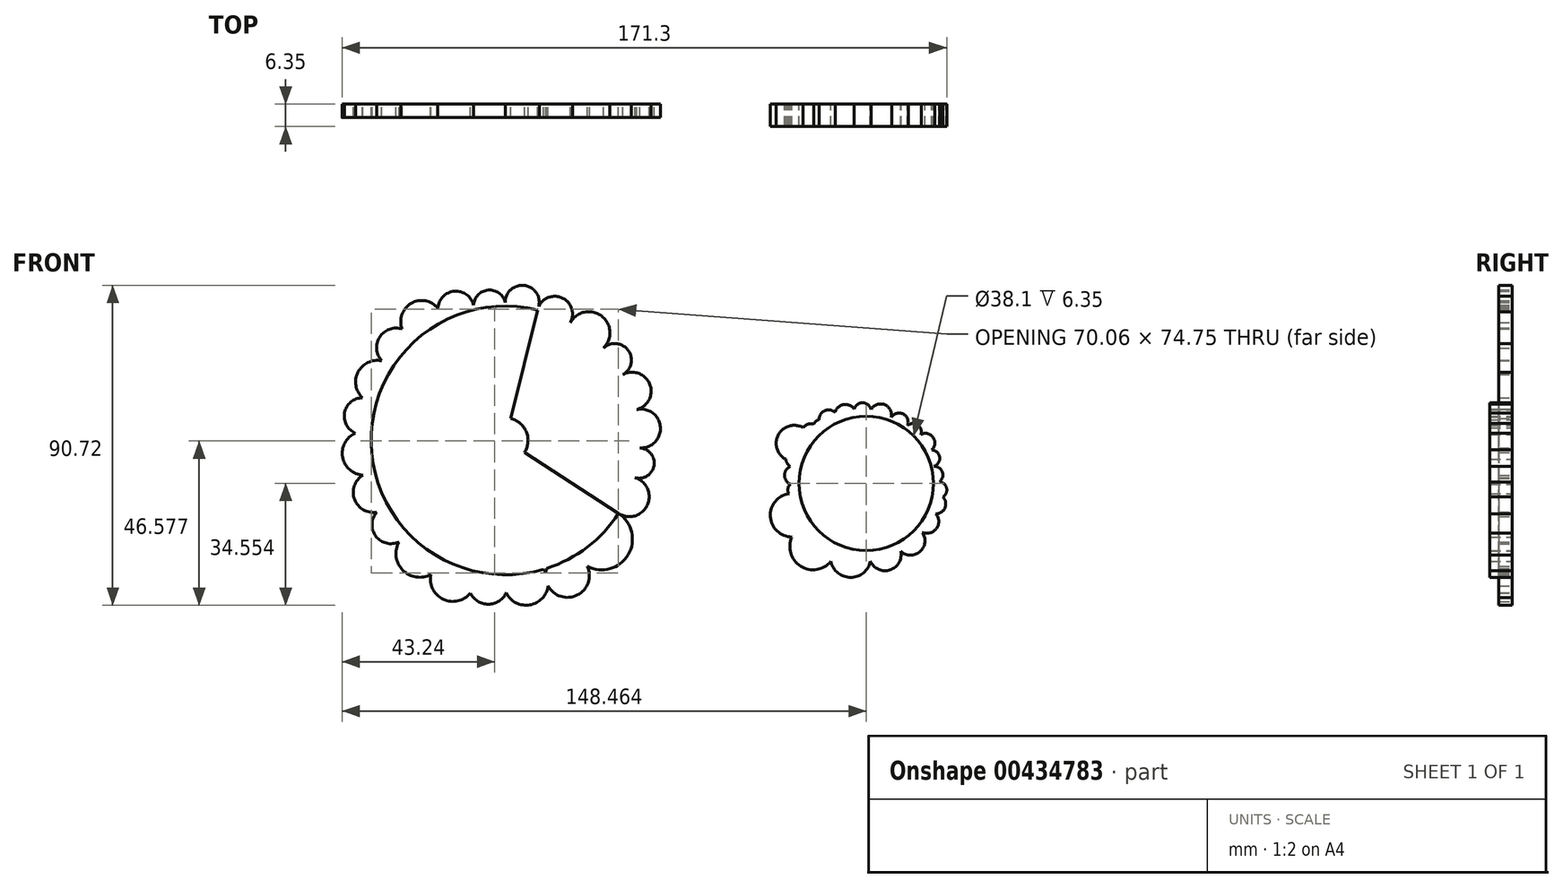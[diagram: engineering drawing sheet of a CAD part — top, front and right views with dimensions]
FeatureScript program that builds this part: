
annotation { "Feature Type Name" : "Feature", "Feature Type Description" : "" }
export const myFeature = defineFeature(function(context is Context, id is Id, definition is map)
    precondition{}
    {
        {
            var Q0;
            Q0=qCreatedBy(makeId("Front.planeOp"),FACE);
            var sketch = newSketch(context, id + "F0", { "sketchPlane" : qUnion([Q0])});
            skCircle(sketch, "E0", {"center": v(-53.83, 43.14) * mm, "radius": 38.1 * mm});
            skCircle(sketch, "E1", {"center": v(-53.83, 43.14) * mm, "radius": 6.35 * mm});
            skLineSegment(sketch, "E2", {"start": v(-71.65, 76.82) * mm, "end": v(-53.83, 43.14) * mm});
            skLineSegment(sketch, "E3", {"start": v(-53.83, 43.14) * mm, "end": v(-34.02, 10.6) * mm});
            skLineSegment(sketch, "E4", {"start": v(-53.83, 43.14) * mm, "end": v(-62.77, 80.18) * mm});
            skLineSegment(sketch, "E5", {"start": v(-53.83, 43.14) * mm, "end": v(-43.1, 6.58) * mm});
            skLineSegment(sketch, "E6", {"start": v(-53.83, 5.04) * mm, "end": v(-53.83, 81.24) * mm});
            skLineSegment(sketch, "E7", {"start": v(-85.76, 63.93) * mm, "end": v(-21.86, 22.42) * mm});
            skLineSegment(sketch, "E8", {"start": v(-44.79, 80.15) * mm, "end": v(-62.86, 6.12) * mm});
            skLineSegment(sketch, "E9", {"start": v(-15.8, 41.02) * mm, "end": v(-91.87, 45.34) * mm});
            skLineSegment(sketch, "E10", {"start": v(-20.61, 61.8) * mm, "end": v(-87.08, 24.54) * mm});
            skLineSegment(sketch, "E11", {"start": v(-90.48, 53.55) * mm, "end": v(-17.23, 32.56) * mm});
            skLineSegment(sketch, "E12", {"start": v(-16.74, 51.85) * mm, "end": v(-90.84, 34.1) * mm});
            skLineSegment(sketch, "E13", {"start": v(-81.45, 16.9) * mm, "end": v(-26.14, 69.3) * mm});
            skLineSegment(sketch, "E14", {"start": v(-72.31, 9.82) * mm, "end": v(-35.5, 76.54) * mm});
            skArc(sketch, "E15", {"start": v(-62.77, 80.18) * mm, "mid": v(-69.71, 85.11) * mm, "end": v(-71.65, 76.82) * mm});
            skArc(sketch, "E16", {"start": v(-44.79, 80.15) * mm, "mid": v(-48.54, 87.07) * mm, "end": v(-53.83, 81.24) * mm});
            skArc(sketch, "E17", {"start": v(-26.14, 69.3) * mm, "mid": v(-26.6, 78.38) * mm, "end": v(-35.5, 76.54) * mm});
            skArc(sketch, "E18", {"start": v(-16.74, 51.85) * mm, "mid": v(-12.98, 59.04) * mm, "end": v(-20.61, 61.8) * mm});
            skArc(sketch, "E19", {"start": v(-71.65, 76.82) * mm, "mid": v(-81.02, 81.72) * mm, "end": v(-79.55, 71.25) * mm});
            skArc(sketch, "E20", {"start": v(-53.83, 81.24) * mm, "mid": v(-58.9, 85.74) * mm, "end": v(-62.77, 80.18) * mm});
            skArc(sketch, "E21", {"start": v(-35.5, 76.54) * mm, "mid": v(-38.08, 83.65) * mm, "end": v(-44.79, 80.15) * mm});
            skArc(sketch, "E22", {"start": v(-20.61, 61.8) * mm, "mid": v(-19.12, 68.68) * mm, "end": v(-26.14, 69.3) * mm});
            skArc(sketch, "E23", {"start": v(-15.8, 41.02) * mm, "mid": v(-9.98, 46.99) * mm, "end": v(-16.74, 51.85) * mm});
            skArc(sketch, "E24", {"start": v(-17.23, 32.56) * mm, "mid": v(-11.79, 35.98) * mm, "end": v(-15.8, 41.02) * mm});
            skArc(sketch, "E25", {"start": v(-21.86, 22.42) * mm, "mid": v(-13.66, 24.8) * mm, "end": v(-17.23, 32.56) * mm});
            skArc(sketch, "E26", {"start": v(-34.02, 10.6) * mm, "mid": v(-20.53, 8.9) * mm, "end": v(-21.86, 22.42) * mm});
            skArc(sketch, "E27", {"start": v(-42.15, 6.87) * mm, "mid": v(-33.7, -0.83) * mm, "end": v(-34.02, 10.6) * mm});
            skArc(sketch, "E28", {"start": v(-53.83, 5.04) * mm, "mid": v(-47.13, -3.55) * mm, "end": v(-43.1, 6.58) * mm});
            skArc(sketch, "E29", {"start": v(-62.86, 6.12) * mm, "mid": v(-59.41, -3.3) * mm, "end": v(-53.83, 5.04) * mm});
            skArc(sketch, "E30", {"start": v(-71.65, 9.46) * mm, "mid": v(-71.02, -2.12) * mm, "end": v(-62.86, 6.12) * mm});
            skArc(sketch, "E31", {"start": v(-81.45, 16.9) * mm, "mid": v(-82.23, 5.7) * mm, "end": v(-71.65, 9.46) * mm});
            skArc(sketch, "E32", {"start": v(-87.08, 24.54) * mm, "mid": v(-90.63, 16.03) * mm, "end": v(-81.45, 16.9) * mm});
            skArc(sketch, "E33", {"start": v(-90.84, 34.1) * mm, "mid": v(-96.59, 26.32) * mm, "end": v(-87.08, 24.54) * mm});
            skArc(sketch, "E34", {"start": v(-91.87, 45.34) * mm, "mid": v(-100.1, 38.92) * mm, "end": v(-90.84, 34.1) * mm});
            skArc(sketch, "E35", {"start": v(-90.48, 53.55) * mm, "mid": v(-99.47, 50.85) * mm, "end": v(-91.87, 45.34) * mm});
            skArc(sketch, "E36", {"start": v(-85.76, 63.93) * mm, "mid": v(-95.77, 62.22) * mm, "end": v(-90.48, 53.55) * mm});
            skArc(sketch, "E37", {"start": v(-79.55, 71.25) * mm, "mid": v(-89.06, 73.02) * mm, "end": v(-85.76, 63.93) * mm});
            skSolve(sketch);
        }
        {
            var Q0;
            Q0=qCreatedBy(makeId("Front.planeOp"),FACE);
            var sketch = newSketch(context, id + "F1", { "sketchPlane" : qUnion([Q0])});
            skCircle(sketch, "E38", {"center": v(48.33, 30.93) * mm, "radius": 19.05 * mm});
            skCircle(sketch, "E39", {"center": v(48.33, 30.93) * mm, "radius": 6.35 * mm});
            skArc(sketch, "E40", {"start": v(45.45, 49.76) * mm, "mid": v(41.56, 53.2) * mm, "end": v(40.24, 48.18) * mm});
            skArc(sketch, "E41", {"start": v(49.32, 49.96) * mm, "mid": v(47.18, 53.8) * mm, "end": v(45.45, 49.76) * mm});
            skArc(sketch, "E42", {"start": v(55.07, 48.75) * mm, "mid": v(53.04, 53.4) * mm, "end": v(49.32, 49.96) * mm});
            skArc(sketch, "E43", {"start": v(59.41, 46.43) * mm, "mid": v(58.84, 50.59) * mm, "end": v(55.07, 48.75) * mm});
            skArc(sketch, "E44", {"start": v(62.66, 43.5) * mm, "mid": v(63.18, 47.33) * mm, "end": v(59.41, 46.43) * mm});
            skArc(sketch, "E45", {"start": v(65.2, 39.8) * mm, "mid": v(67.3, 43.97) * mm, "end": v(62.66, 43.5) * mm});
            skArc(sketch, "E46", {"start": v(66.79, 35.67) * mm, "mid": v(69.01, 38.9) * mm, "end": v(65.2, 39.8) * mm});
            skArc(sketch, "E47", {"start": v(67.38, 30.83) * mm, "mid": v(70.02, 33.61) * mm, "end": v(66.79, 35.67) * mm});
            skArc(sketch, "E48", {"start": v(67.1, 27.64) * mm, "mid": v(71.16, 28.88) * mm, "end": v(67.38, 30.83) * mm});
            skArc(sketch, "E49", {"start": v(65.87, 23.48) * mm, "mid": v(70.76, 24.3) * mm, "end": v(67.1, 27.64) * mm});
            skArc(sketch, "E50", {"start": v(62.66, 18.38) * mm, "mid": v(68.36, 18.35) * mm, "end": v(65.87, 23.48) * mm});
            skArc(sketch, "E51", {"start": v(56.9, 13.92) * mm, "mid": v(63.4, 11.45) * mm, "end": v(62.66, 18.38) * mm});
            skArc(sketch, "E52", {"start": v(49.32, 11.9) * mm, "mid": v(54.85, 6.33) * mm, "end": v(56.9, 13.92) * mm});
            skArc(sketch, "E53", {"start": v(39.77, 13.92) * mm, "mid": v(42.76, 4.4) * mm, "end": v(49.32, 11.9) * mm});
            skArc(sketch, "E54", {"start": v(33.03, 19.6) * mm, "mid": v(29.02, 8) * mm, "end": v(39.77, 13.92) * mm});
            skArc(sketch, "E55", {"start": v(29.57, 27.64) * mm, "mid": v(21.66, 19.48) * mm, "end": v(33.03, 19.6) * mm});
            skArc(sketch, "E56", {"start": v(29.28, 30.83) * mm, "mid": v(26.13, 28.94) * mm, "end": v(29.57, 27.64) * mm});
            skArc(sketch, "E57", {"start": v(29.28, 35.67) * mm, "mid": v(25.2, 33.25) * mm, "end": v(29.28, 30.83) * mm});
            skArc(sketch, "E58", {"start": v(30.63, 37.97) * mm, "mid": v(25.93, 39.17) * mm, "end": v(29.28, 35.67) * mm});
            skArc(sketch, "E59", {"start": v(33.03, 42.27) * mm, "mid": v(23.46, 44.78) * mm, "end": v(30.63, 37.97) * mm});
            skArc(sketch, "E60", {"start": v(35.58, 45.09) * mm, "mid": v(30.69, 46.97) * mm, "end": v(33.03, 42.27) * mm});
            skArc(sketch, "E61", {"start": v(37.26, 46.43) * mm, "mid": v(34.13, 48.6) * mm, "end": v(35.58, 45.09) * mm});
            skArc(sketch, "E62", {"start": v(40.24, 48.18) * mm, "mid": v(36.34, 51.42) * mm, "end": v(37.26, 46.43) * mm});
            skSolve(sketch);
        }
        {
            var Q0;
            Q0 = qSketchRegion(id + "F1", true);
            extrude(context, id + "F2", {"entities" : qUnion([Q0]), "depth" : 6.35 * mm});
        }
        {
            var Q0;
            Q0 = qSketchRegion(id + "F0", true);
            extrude(context, id + "F3", {"entities" : qUnion([Q0]), "depth" : 3.8 * mm});
        }
    });
